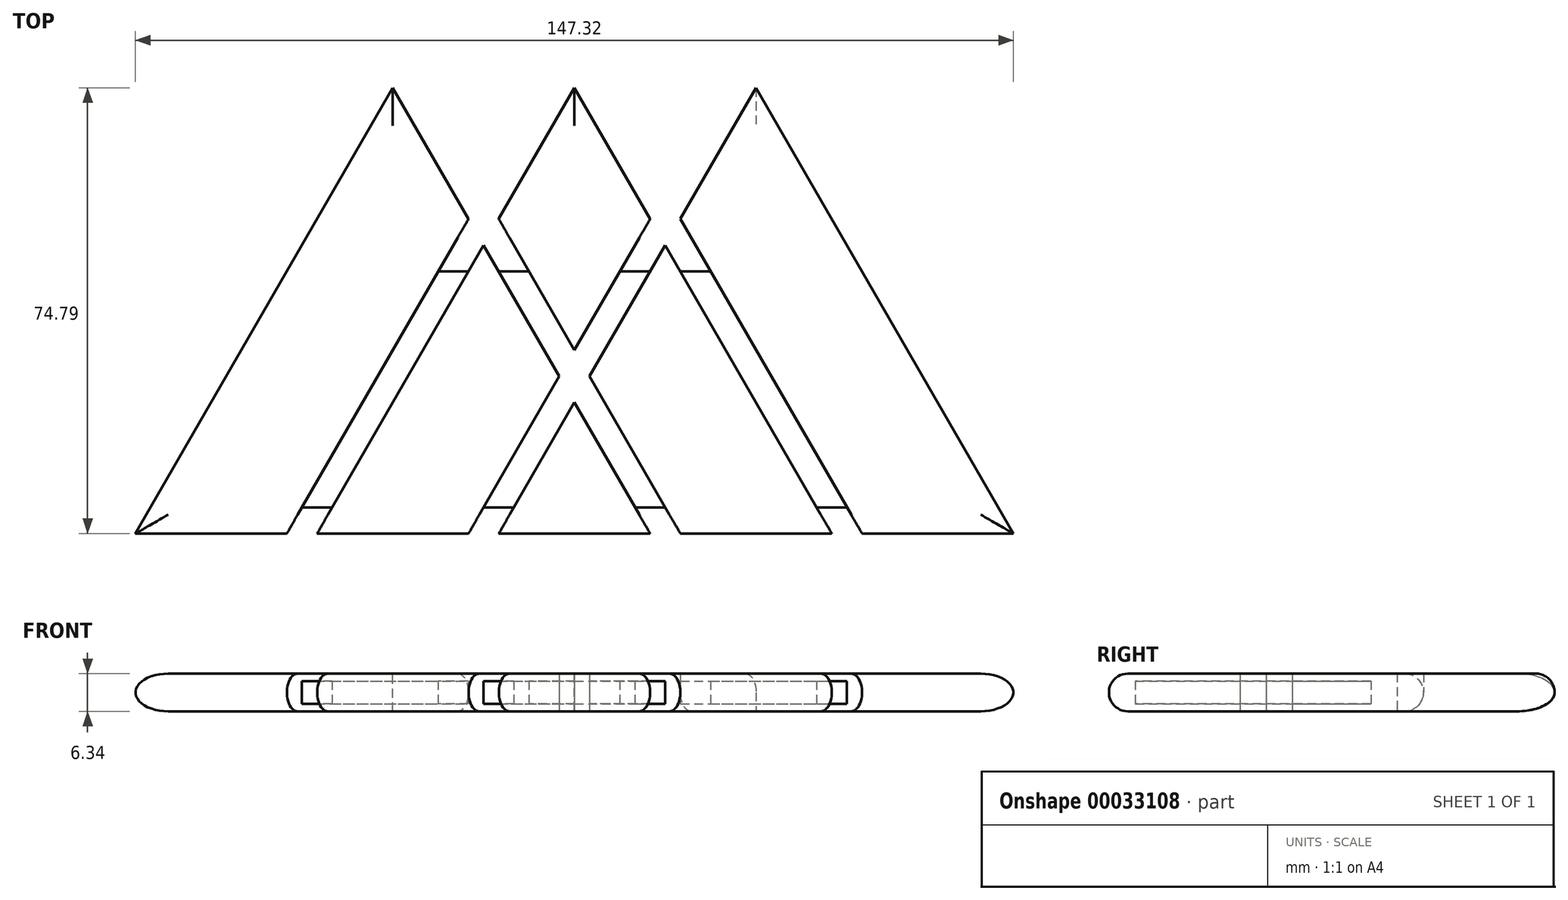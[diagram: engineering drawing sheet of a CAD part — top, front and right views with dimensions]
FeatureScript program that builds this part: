
annotation { "Feature Type Name" : "Feature", "Feature Type Description" : "" }
export const myFeature = defineFeature(function(context is Context, id is Id, definition is map)
    precondition{}
    {
        {
            var Q0;
            Q0=qCreatedBy(makeId("Top.planeOp"),FACE);
            var sketch = newSketch(context, id + "F0", { "sketchPlane" : qUnion([Q0])});
            skLineSegment(sketch, "E0", {"start": v(0, 0) * mm, "end": v(25.4, 0) * mm});
            skLineSegment(sketch, "E1", {"start": v(30.48, 0) * mm, "end": v(55.88, 0) * mm});
            skLineSegment(sketch, "E2", {"start": v(60.96, 0) * mm, "end": v(86.36, 0) * mm});
            skLineSegment(sketch, "E3", {"start": v(91.44, 0) * mm, "end": v(116.84, 0) * mm});
            skLineSegment(sketch, "E4", {"start": v(121.92, 0) * mm, "end": v(147.32, 0) * mm});
            skLineSegment(sketch, "E5", {"start": v(60.96, 0) * mm, "end": v(73.66, 22) * mm});
            skPoint(sketch, "E5.endSnap0", {"position": v(73.66, 0) * mm});
            skLineSegment(sketch, "E6", {"start": v(73.66, 22) * mm, "end": v(86.36, 0) * mm});
            skLineSegment(sketch, "E7", {"start": v(91.44, 0) * mm, "end": v(76.2, 26.4) * mm});
            skLineSegment(sketch, "E8", {"start": v(88.9, 48.4) * mm, "end": v(116.84, 0) * mm});
            skLineSegment(sketch, "E9", {"start": v(88.9, 48.4) * mm, "end": v(76.2, 26.4) * mm});
            skLineSegment(sketch, "E10", {"start": v(91.44, 52.8) * mm, "end": v(121.92, 0) * mm});
            skLineSegment(sketch, "E11", {"start": v(91.44, 52.8) * mm, "end": v(104.14, 74.79) * mm});
            skLineSegment(sketch, "E12", {"start": v(104.14, 74.79) * mm, "end": v(147.32, 0) * mm});
            skLineSegment(sketch, "E13", {"start": v(55.88, 0) * mm, "end": v(71.12, 26.4) * mm});
            skLineSegment(sketch, "E14", {"start": v(30.48, 0) * mm, "end": v(58.42, 48.4) * mm});
            skLineSegment(sketch, "E15", {"start": v(25.4, 0) * mm, "end": v(55.88, 52.8) * mm});
            skLineSegment(sketch, "E16", {"start": v(0, 0) * mm, "end": v(43.18, 74.79) * mm});
            skLineSegment(sketch, "E17", {"start": v(73.66, 30.8) * mm, "end": v(86.36, 52.8) * mm});
            skLineSegment(sketch, "E18", {"start": v(73.66, 30.8) * mm, "end": v(60.96, 52.8) * mm});
            skLineSegment(sketch, "E19", {"start": v(86.36, 52.8) * mm, "end": v(73.66, 74.79) * mm});
            skLineSegment(sketch, "E20", {"start": v(60.96, 52.8) * mm, "end": v(73.66, 74.79) * mm});
            skLineSegment(sketch, "E21", {"start": v(43.18, 74.79) * mm, "end": v(55.88, 52.8) * mm});
            skLineSegment(sketch, "E22", {"start": v(58.42, 48.4) * mm, "end": v(71.12, 26.4) * mm});
            skLineSegment(sketch, "E23", {"start": v(116.84, 0) * mm, "end": v(114.3, 4.4) * mm});
            skLineSegment(sketch, "E24", {"start": v(114.3, 4.4) * mm, "end": v(119.38, 4.4) * mm});
            skLineSegment(sketch, "E25", {"start": v(86.36, 0) * mm, "end": v(83.82, 4.4) * mm});
            skLineSegment(sketch, "E26", {"start": v(83.82, 4.4) * mm, "end": v(88.9, 4.4) * mm});
            skLineSegment(sketch, "E27", {"start": v(60.96, 0) * mm, "end": v(63.5, 4.4) * mm});
            skLineSegment(sketch, "E28", {"start": v(63.5, 4.4) * mm, "end": v(58.42, 4.4) * mm});
            skLineSegment(sketch, "E29", {"start": v(30.48, 0) * mm, "end": v(33.02, 4.4) * mm});
            skLineSegment(sketch, "E30", {"start": v(33.02, 4.4) * mm, "end": v(27.94, 4.4) * mm});
            skLineSegment(sketch, "E31", {"start": v(88.9, 48.4) * mm, "end": v(91.44, 44) * mm});
            skLineSegment(sketch, "E32", {"start": v(91.44, 44) * mm, "end": v(96.52, 44) * mm});
            skLineSegment(sketch, "E33", {"start": v(88.9, 48.4) * mm, "end": v(86.36, 44) * mm});
            skLineSegment(sketch, "E34", {"start": v(86.36, 44) * mm, "end": v(81.28, 44) * mm});
            skLineSegment(sketch, "E35", {"start": v(58.42, 48.4) * mm, "end": v(60.96, 44) * mm});
            skLineSegment(sketch, "E36", {"start": v(60.96, 44) * mm, "end": v(66.04, 44) * mm});
            skLineSegment(sketch, "E37", {"start": v(58.42, 48.4) * mm, "end": v(55.88, 44) * mm});
            skLineSegment(sketch, "E38", {"start": v(55.88, 44) * mm, "end": v(50.8, 44) * mm});
            skSolve(sketch);
        }
        {
            var Q0;
            {var subQ4=sQuery(id+"F0.wireOp",EDGE,"E0");Q0=makeQuery(id+"F0.imprint","IMPRINT",FACE,{"disambiguationData":[TD([[makeQuery(id+"F0.imprint","IMPRINT",EDGE,{"derivedFrom":subQ4}),1.0]])]});}
            var Q1;
            {var subQ3=sQuery(id+"F0.wireOp",EDGE,"E1");Q1=makeQuery(id+"F0.imprint","IMPRINT",FACE,{"disambiguationData":[TD([[makeQuery(id+"F0.imprint","IMPRINT",EDGE,{"derivedFrom":subQ3}),1.0]])]});}
            var Q2;
            {var subQ1=sQuery(id+"F0.wireOp",EDGE,"E19");Q2=makeQuery(id+"F0.imprint","IMPRINT",FACE,{"disambiguationData":[TD([[makeQuery(id+"F0.imprint","IMPRINT",EDGE,{"derivedFrom":subQ1}),1.0]])]});}
            var Q3;
            {var subQ3=sQuery(id+"F0.wireOp",EDGE,"E3");Q3=makeQuery(id+"F0.imprint","IMPRINT",FACE,{"disambiguationData":[TD([[makeQuery(id+"F0.imprint","IMPRINT",EDGE,{"derivedFrom":subQ3}),1.0]])]});}
            var Q4;
            Q4=makeQuery(id+"F0.imprint","IMPRINT",FACE,{"disambiguationData":[TD([[makeQuery(id+"F0.imprint","IMPRINT",EDGE,{"derivedFrom":sQuery(id+"F0.wireOp",EDGE,"E2")}),1.0]])]});
            var Q5;
            {var subQ3=sQuery(id+"F0.wireOp",EDGE,"E4");Q5=makeQuery(id+"F0.imprint","IMPRINT",FACE,{"disambiguationData":[TD([[makeQuery(id+"F0.imprint","IMPRINT",EDGE,{"derivedFrom":subQ3}),1.0]])]});}
            extrude(context, id + "F1", {"entities" : qUnion([Q0, Q1, Q2, Q3, Q4, Q5]), "endBound" : BoundingType.SYMMETRIC, "depth" : 6.35 * mm});
        }
        {
            var Q0;
            Q0=makeQuery(id+"F0.imprint","IMPRINT",FACE,{"disambiguationData":[TD([[makeQuery(id+"F0.imprint","IMPRINT",EDGE,{"derivedFrom":sQuery(id+"F0.wireOp",EDGE,"E8")}),1.0]])]});
            var Q1;
            Q1=makeQuery(id+"F0.imprint","IMPRINT",FACE,{"disambiguationData":[TD([[makeQuery(id+"F0.imprint","IMPRINT",EDGE,{"derivedFrom":sQuery(id+"F0.wireOp",EDGE,"E5")}),1.0]])]});
            var Q2;
            Q2=makeQuery(id+"F0.imprint","IMPRINT",FACE,{"disambiguationData":[TD([[makeQuery(id+"F0.imprint","IMPRINT",EDGE,{"derivedFrom":sQuery(id+"F0.wireOp",EDGE,"E14")}),1.0]])]});
            extrude(context, id + "F2", {"entities" : qUnion([Q0, Q1, Q2]), "endBound" : BoundingType.SYMMETRIC, "depth" : 3.8 * mm});
        }
        {
            var Q0;
            Q0=makeQuery(id+"F1.opExtrude","CAP_EDGE",EDGE,{"disambiguationData":[OSD([sQuery(id+"F0.wireOp",EDGE,"E16")])],"isStart":false});
            var Q1;
            Q1=makeQuery(id+"F1.opExtrude","CAP_EDGE",EDGE,{"disambiguationData":[OSD([sQuery(id+"F0.wireOp",EDGE,"E16")])],"isStart":true});
            var Q2;
            Q2=makeQuery(id+"F1.opExtrude","CAP_EDGE",EDGE,{"disambiguationData":[OSD([sQuery(id+"F0.wireOp",EDGE,"E20")])],"isStart":false});
            var Q3;
            Q3=makeQuery(id+"F1.opExtrude","CAP_EDGE",EDGE,{"disambiguationData":[OSD([sQuery(id+"F0.wireOp",EDGE,"E19")])],"isStart":false});
            var Q4;
            Q4=makeQuery(id+"F1.opExtrude","CAP_EDGE",EDGE,{"disambiguationData":[OSD([sQuery(id+"F0.wireOp",EDGE,"E19")])],"isStart":true});
            var Q5;
            Q5=makeQuery(id+"F1.opExtrude","CAP_EDGE",EDGE,{"disambiguationData":[OSD([sQuery(id+"F0.wireOp",EDGE,"E20")])],"isStart":true});
            var Q6;
            Q6=makeQuery(id+"F1.opExtrude","CAP_EDGE",EDGE,{"disambiguationData":[OSD([sQuery(id+"F0.wireOp",EDGE,"E0")])],"isStart":true});
            var Q7;
            Q7=makeQuery(id+"F1.opExtrude","CAP_EDGE",EDGE,{"disambiguationData":[OSD([sQuery(id+"F0.wireOp",EDGE,"E1")])],"isStart":true});
            var Q8;
            Q8=makeQuery(id+"F1.opExtrude","CAP_EDGE",EDGE,{"disambiguationData":[OSD([sQuery(id+"F0.wireOp",EDGE,"E2")])],"isStart":true});
            var Q9;
            Q9=makeQuery(id+"F1.opExtrude","CAP_EDGE",EDGE,{"disambiguationData":[OSD([sQuery(id+"F0.wireOp",EDGE,"E3")])],"isStart":true});
            var Q10;
            Q10=makeQuery(id+"F1.opExtrude","CAP_EDGE",EDGE,{"disambiguationData":[OSD([sQuery(id+"F0.wireOp",EDGE,"E4")])],"isStart":true});
            var Q11;
            Q11=makeQuery(id+"F1.opExtrude","CAP_EDGE",EDGE,{"disambiguationData":[OSD([sQuery(id+"F0.wireOp",EDGE,"E12")])],"isStart":true});
            var Q12;
            Q12=makeQuery(id+"F1.opExtrude","CAP_EDGE",EDGE,{"disambiguationData":[OSD([sQuery(id+"F0.wireOp",EDGE,"E11")])],"isStart":true});
            var Q13;
            Q13=makeQuery(id+"F1.opExtrude","CAP_EDGE",EDGE,{"disambiguationData":[OSD([sQuery(id+"F0.wireOp",EDGE,"E0")])],"isStart":false});
            var Q14;
            Q14=makeQuery(id+"F1.opExtrude","CAP_EDGE",EDGE,{"disambiguationData":[OSD([sQuery(id+"F0.wireOp",EDGE,"E1")])],"isStart":false});
            var Q15;
            Q15=makeQuery(id+"F1.opExtrude","CAP_EDGE",EDGE,{"disambiguationData":[OSD([sQuery(id+"F0.wireOp",EDGE,"E2")])],"isStart":false});
            var Q16;
            Q16=makeQuery(id+"F1.opExtrude","CAP_EDGE",EDGE,{"disambiguationData":[OSD([sQuery(id+"F0.wireOp",EDGE,"E3")])],"isStart":false});
            var Q17;
            Q17=makeQuery(id+"F1.opExtrude","CAP_EDGE",EDGE,{"disambiguationData":[OSD([sQuery(id+"F0.wireOp",EDGE,"E4")])],"isStart":false});
            var Q18;
            Q18=makeQuery(id+"F1.opExtrude","CAP_EDGE",EDGE,{"disambiguationData":[OSD([sQuery(id+"F0.wireOp",EDGE,"E12")])],"isStart":false});
            var Q19;
            Q19=makeQuery(id+"F1.opExtrude","CAP_EDGE",EDGE,{"disambiguationData":[OSD([sQuery(id+"F0.wireOp",EDGE,"E21")])],"isStart":false});
            var Q20;
            Q20=makeQuery(id+"F1.opExtrude","CAP_EDGE",EDGE,{"disambiguationData":[OSD([sQuery(id+"F0.wireOp",EDGE,"E21")])],"isStart":true});
            fillet(context, id + "F3", {"entities" : qUnion([Q0, Q1, Q2, Q3, Q4, Q5, Q6, Q7, Q8, Q9, Q10, Q11, Q12, Q13, Q14, Q15, Q16, Q17, Q18, Q19, Q20]), "radius" : 3.17 * mm, "tangentPropagation" : true, "allowEdgeOverflow" : false});
        }
    });
